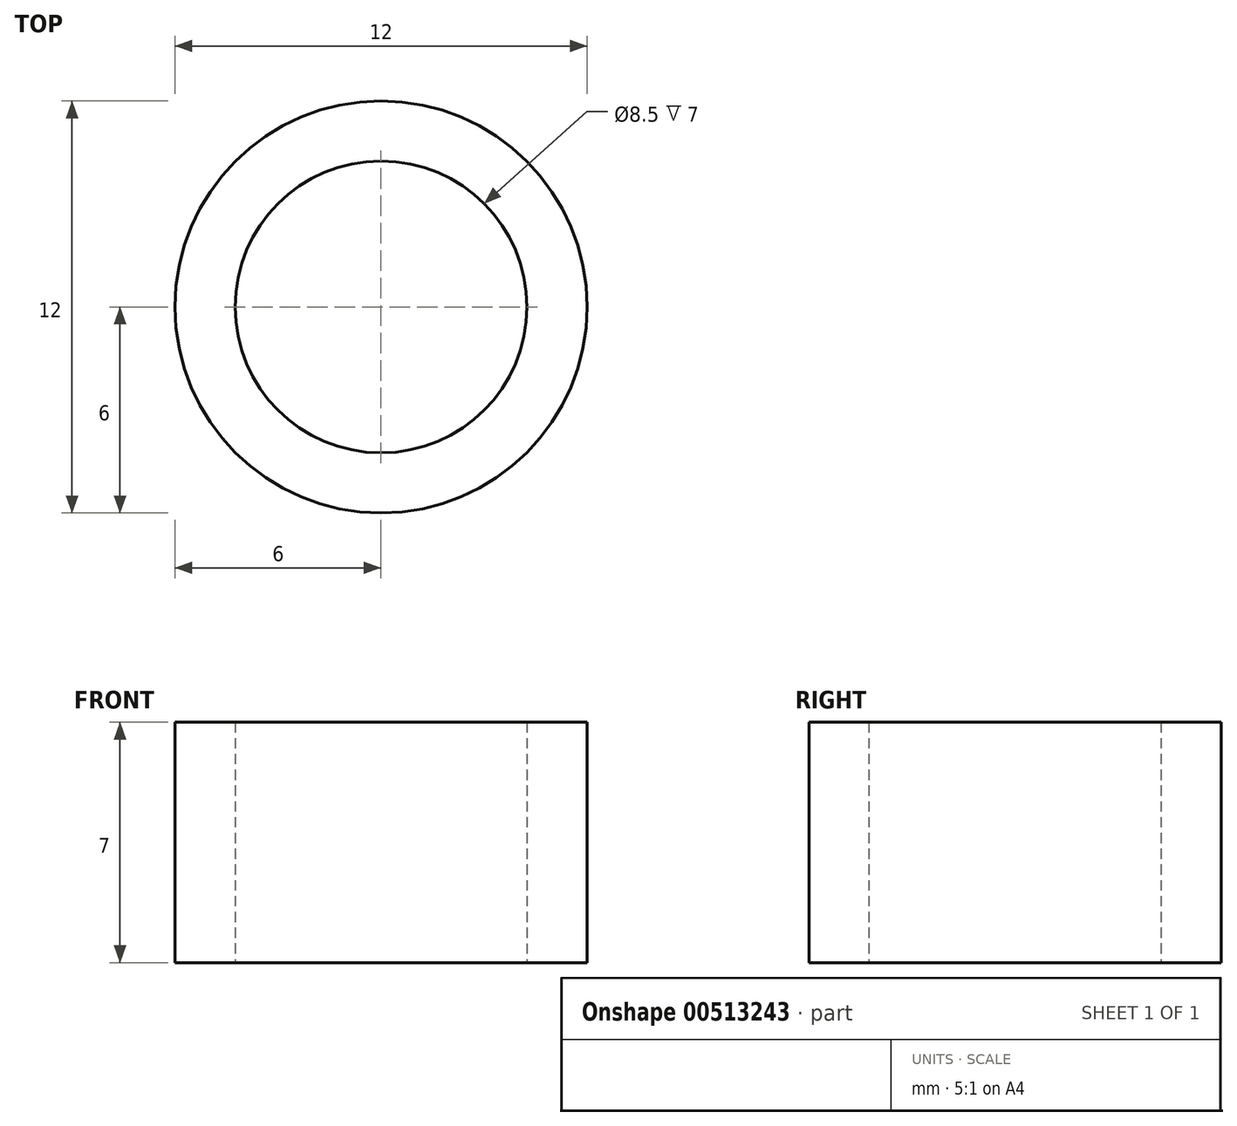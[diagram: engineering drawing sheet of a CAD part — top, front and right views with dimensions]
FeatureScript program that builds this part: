
annotation { "Feature Type Name" : "Feature", "Feature Type Description" : "" }
export const myFeature = defineFeature(function(context is Context, id is Id, definition is map)
    precondition{}
    {
        {
            var Q0;
            Q0=qCreatedBy(makeId("Top.planeOp"),FACE);
            var sketch = newSketch(context, id + "F0", { "sketchPlane" : qUnion([Q0])});
            skCircle(sketch, "E0", {"center": v(0, 0) * mm, "radius": 6 * mm});
            skCircle(sketch, "E1", {"center": v(0, 0) * mm, "radius": 4.25 * mm});
            skSolve(sketch);
        }
        {
            var Q0;
            Q0=qSketchRegion(id+"F0",true);
            extrude(context, id + "F1", {"entities" : qUnion([Q0]), "depth" : 7 * mm, "offsetDistance" : 25 * mm});
        }
    });
